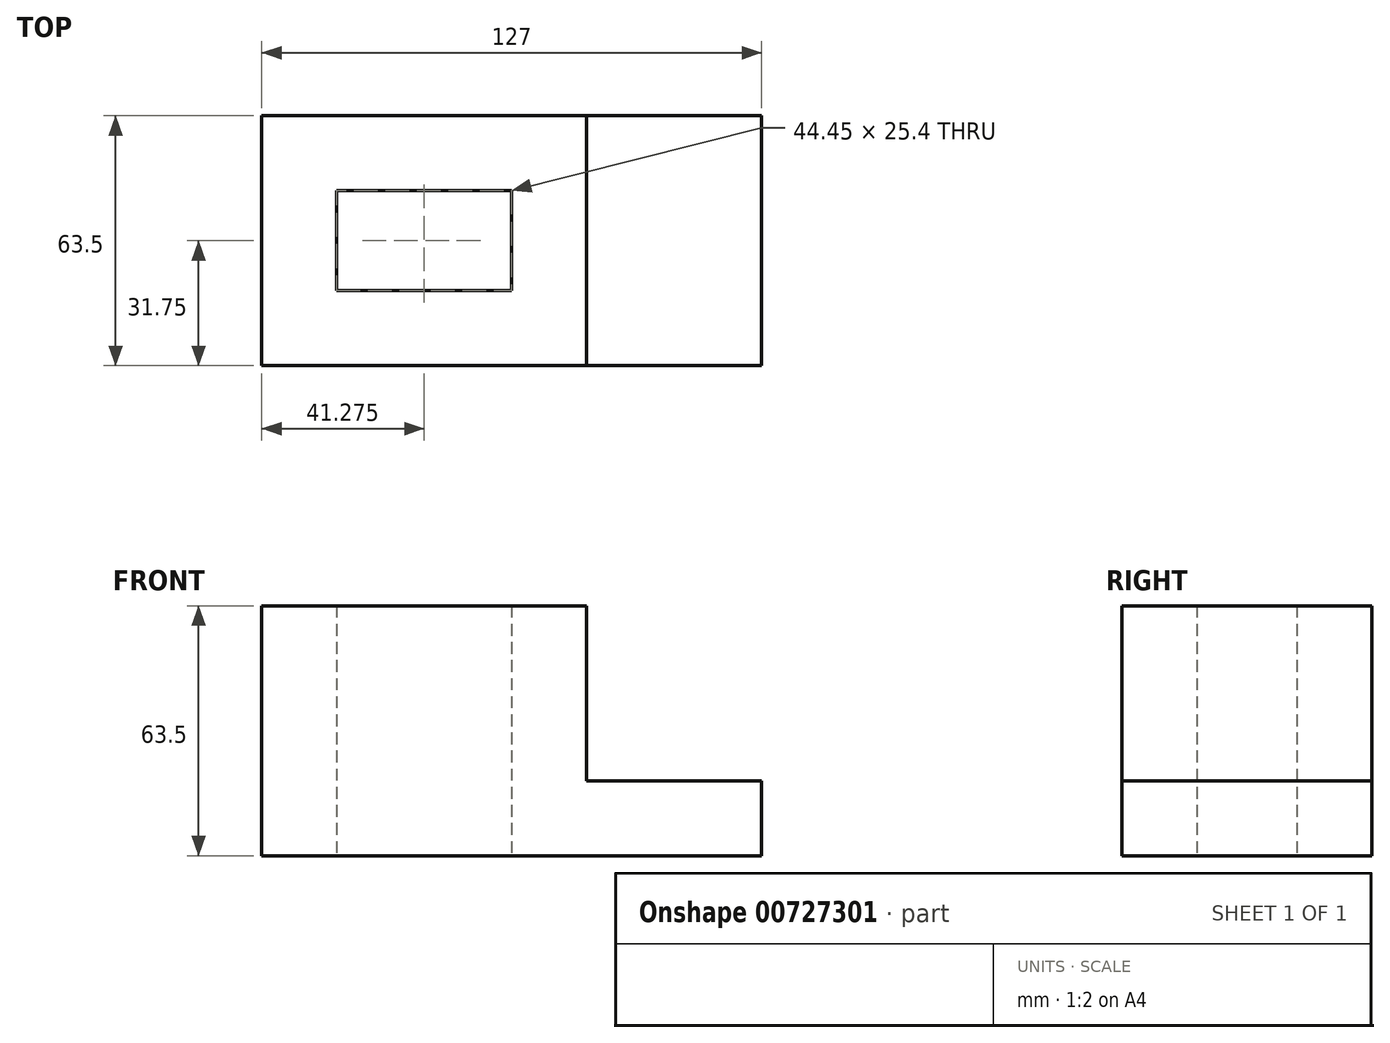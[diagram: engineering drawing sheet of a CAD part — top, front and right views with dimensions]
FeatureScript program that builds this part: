
annotation { "Feature Type Name" : "Feature", "Feature Type Description" : "" }
export const myFeature = defineFeature(function(context is Context, id is Id, definition is map)
    precondition{}
    {
        {
            var Q0;
            Q0=qCreatedBy(makeId("Front.planeOp"),FACE);
            var sketch = newSketch(context, id + "F0", { "sketchPlane" : qUnion([Q0])});
            skLineSegment(sketch, "E0", {"start": v(0, 0) * mm, "end": v(44.45, 0) * mm});
            skLineSegment(sketch, "E1", {"start": v(44.45, 0) * mm, "end": v(44.45, 19.05) * mm});
            skLineSegment(sketch, "E2", {"start": v(44.45, 19.05) * mm, "end": v(0, 19.05) * mm});
            skLineSegment(sketch, "E3", {"start": v(0, 19.05) * mm, "end": v(0, 63.5) * mm});
            skLineSegment(sketch, "E4", {"start": v(0, 63.5) * mm, "end": v(-82.55, 63.5) * mm});
            skLineSegment(sketch, "E5", {"start": v(-82.55, 0) * mm, "end": v(0, 0) * mm});
            skLineSegment(sketch, "E6", {"start": v(-82.55, 63.5) * mm, "end": v(-82.55, 0) * mm});
            skSolve(sketch);
        }
        {
            var Q0;
            Q0=qCreatedBy(makeId("Top.planeOp"),FACE);
            var sketch = newSketch(context, id + "F1", { "sketchPlane" : qUnion([Q0])});
            skLineSegment(sketch, "E7", {"start": v(-82.55, 0) * mm, "end": v(-82.55, 63.5) * mm});
            skLineSegment(sketch, "E8", {"start": v(-82.55, 63.5) * mm, "end": v(0, 63.5) * mm});
            skLineSegment(sketch, "E9", {"start": v(0, 63.5) * mm, "end": v(0, 0) * mm});
            skLineSegment(sketch, "E10", {"start": v(0, 0) * mm, "end": v(44.45, 0) * mm});
            skLineSegment(sketch, "E11", {"start": v(44.45, 0) * mm, "end": v(44.45, 63.5) * mm});
            skLineSegment(sketch, "E12", {"start": v(44.45, 63.5) * mm, "end": v(0, 63.5) * mm});
            skLineSegment(sketch, "E13", {"start": v(-63.5, 44.45) * mm, "end": v(-63.5, 19.05) * mm});
            skLineSegment(sketch, "E14", {"start": v(-63.5, 19.05) * mm, "end": v(-19.05, 19.05) * mm});
            skLineSegment(sketch, "E15", {"start": v(-19.05, 19.05) * mm, "end": v(-19.05, 44.45) * mm});
            skLineSegment(sketch, "E16", {"start": v(-19.05, 44.45) * mm, "end": v(-63.5, 44.45) * mm});
            skLineSegment(sketch, "E17", {"start": v(-82.55, 0) * mm, "end": v(0, 0) * mm});
            skSolve(sketch);
        }
        {
            var Q0;
            Q0 = qSketchRegion(id + "F0", true);
            extrude(context, id + "F2", {"entities" : qUnion([Q0]), "oppositeDirection" : true, "depth" : 63.5 * mm, "offsetDistance" : 25.4 * mm});
        }
        {
            var Q0;
            Q0=makeQuery(id+"F1.imprint","IMPRINT",FACE,{"disambiguationData":[TD([[makeQuery(id+"F1.imprint","IMPRINT",EDGE,{"derivedFrom":sQuery(id+"F1.wireOp",EDGE,"E13")}),1.0]])]});
            extrude(context, id + "F3", {"entities" : qUnion([Q0]), "operationType" : NewBodyOperationType.REMOVE, "depth" : 63.5 * mm, "offsetDistance" : 25.4 * mm});
        }
    });
